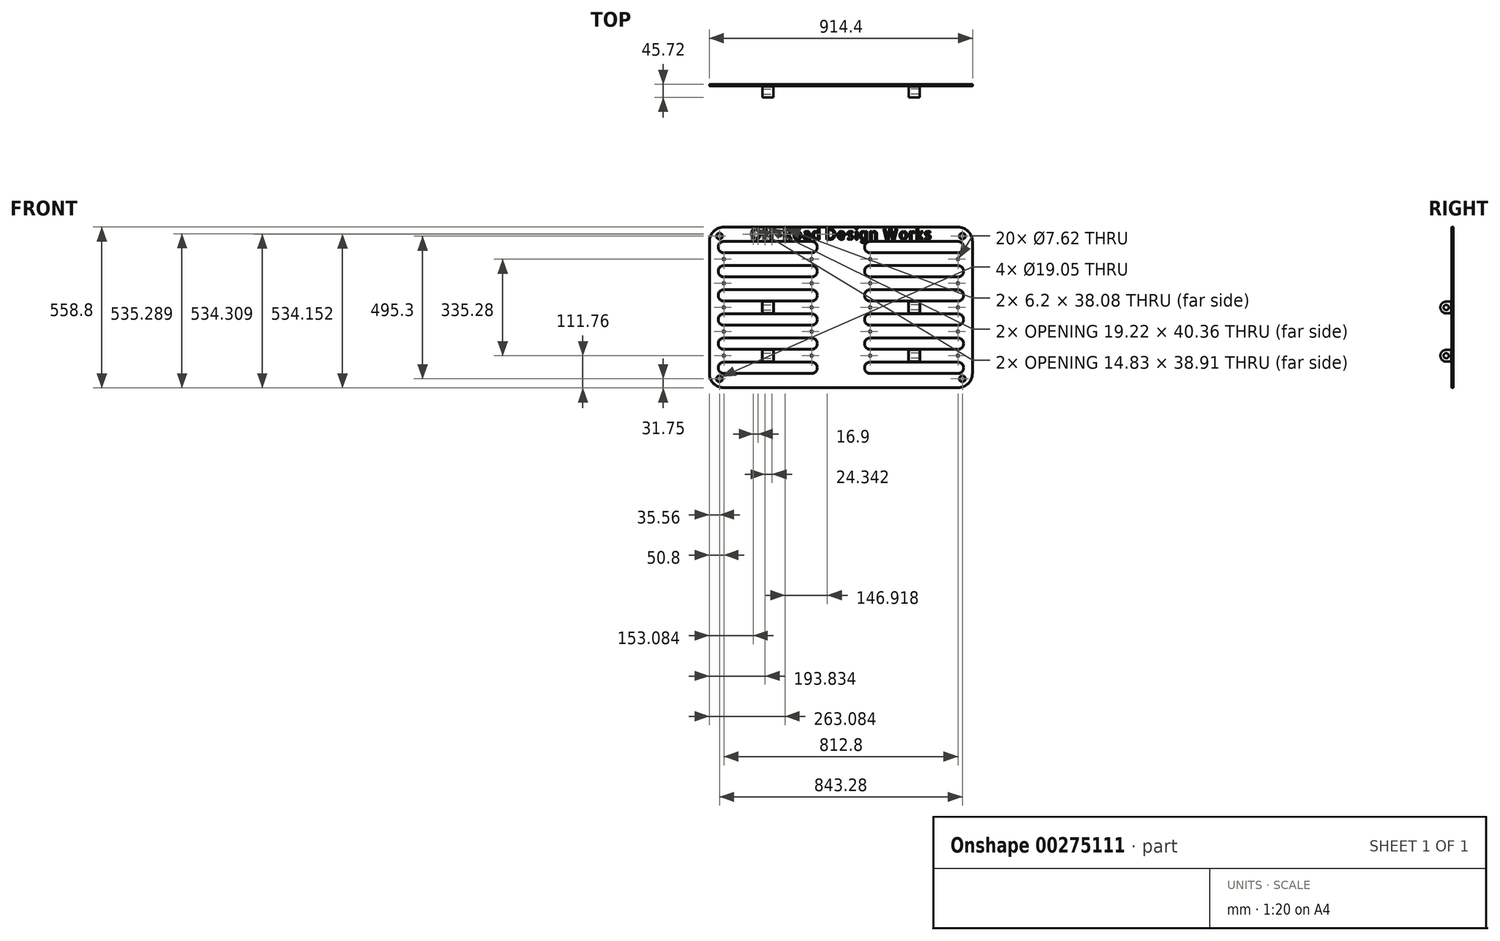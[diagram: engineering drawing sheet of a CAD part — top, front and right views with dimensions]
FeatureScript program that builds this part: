
annotation { "Feature Type Name" : "Feature", "Feature Type Description" : "" }
export const myFeature = defineFeature(function(context is Context, id is Id, definition is map)
    precondition{}
    {
        {
            var Q0;
            Q0=qCreatedBy(makeId("Front.planeOp"),FACE);
            var sketch = newSketch(context, id + "F0", { "sketchPlane" : qUnion([Q0])});
            skLineSegment(sketch, "E0.bottom", {"start": v(406.4, -279.4) * mm, "end": v(-406.4, -279.4) * mm});
            skLineSegment(sketch, "E0.top", {"start": v(406.4, 279.4) * mm, "end": v(-406.4, 279.4) * mm});
            skLineSegment(sketch, "E0.left", {"start": v(457.2, -228.6) * mm, "end": v(457.2, 228.6) * mm});
            skLineSegment(sketch, "E0.right", {"start": v(-457.2, -228.6) * mm, "end": v(-457.2, 228.6) * mm});
            skPoint(sketch, "E0.middle", {"position": v(0, 0) * mm});
            skPoint(sketch, "E1.visualSharp", {"position": v(457.2, 279.4) * mm});
            skArc(sketch, "E1.filletArc", {"start": v(457.2, 228.6) * mm, "mid": v(442.32, 264.52) * mm, "end": v(406.4, 279.4) * mm});
            skPoint(sketch, "E2.visualSharp", {"position": v(-457.2, 279.4) * mm});
            skArc(sketch, "E2.filletArc", {"start": v(-406.4, 279.4) * mm, "mid": v(-442.32, 264.52) * mm, "end": v(-457.2, 228.6) * mm});
            skPoint(sketch, "E3.visualSharp", {"position": v(-457.2, -279.4) * mm});
            skArc(sketch, "E3.filletArc", {"start": v(-457.2, -228.6) * mm, "mid": v(-442.32, -264.52) * mm, "end": v(-406.4, -279.4) * mm});
            skPoint(sketch, "E4.visualSharp", {"position": v(457.2, -279.4) * mm});
            skArc(sketch, "E4.filletArc", {"start": v(406.4, -279.4) * mm, "mid": v(442.32, -264.52) * mm, "end": v(457.2, -228.6) * mm});
            skSolve(sketch);
        }
        {
            var Q0;
            Q0 = qSketchRegion(id + "F0", true);
            extrude(context, id + "F1", {"entities" : qUnion([Q0]), "oppositeDirection" : true, "depth" : 6.35 * mm});
        }
        {
            var Q0;
            Q0=makeQuery(id+"F1.opExtrude","CAP_FACE",FACE,{"disambiguationData":[OSD([sQuery(id+"F0.wireOp",EDGE,"E0.bottom"),sQuery(id+"F0.wireOp",EDGE,"E0.top"),sQuery(id+"F0.wireOp",EDGE,"E0.left"),sQuery(id+"F0.wireOp",EDGE,"E0.right"),sQuery(id+"F0.wireOp",EDGE,"E1.filletArc"),sQuery(id+"F0.wireOp",EDGE,"E2.filletArc"),sQuery(id+"F0.wireOp",EDGE,"E3.filletArc"),sQuery(id+"F0.wireOp",EDGE,"E4.filletArc")])],"isStart":true});
            var sketch = newSketch(context, id + "F2", { "sketchPlane" : qUnion([Q0])});
            skLineSegment(sketch, "E5", {"start": v(0, 0) * mm, "end": v(0, -438.1) * mm, "construction": true});
            skPoint(sketch, "E5.endSnap0", {"position": v(0, -279.4) * mm});
            skLineSegment(sketch, "E6", {"start": v(101.6, 228.6) * mm, "end": v(406.4, 228.6) * mm});
            skArc(sketch, "E7", {"start": v(101.6, 228.6) * mm, "mid": v(82.55, 209.55) * mm, "end": v(101.6, 190.5) * mm});
            skLineSegment(sketch, "E8", {"start": v(101.6, 190.5) * mm, "end": v(406.4, 190.5) * mm});
            skLineSegment(sketch, "E9", {"start": v(254, 228.6) * mm, "end": v(254, 415.14) * mm, "construction": true});
            skPoint(sketch, "E9.endSnap0", {"position": v(254, 190.5) * mm});
            skArc(sketch, "E10.MirrorCS", {"start": v(406.4, 228.6) * mm, "mid": v(425.45, 209.55) * mm, "end": v(406.4, 190.5) * mm});
            skLineSegment(sketch, "E11.0.1.0", {"start": v(101.6, 106.68) * mm, "end": v(406.4, 106.68) * mm});
            skArc(sketch, "E11.0.1.1", {"start": v(101.6, 144.78) * mm, "mid": v(82.55, 125.73) * mm, "end": v(101.6, 106.68) * mm});
            skArc(sketch, "E11.0.1.2", {"start": v(406.4, 144.78) * mm, "mid": v(425.45, 125.73) * mm, "end": v(406.4, 106.68) * mm});
            skLineSegment(sketch, "E11.0.1.3", {"start": v(101.6, 144.78) * mm, "end": v(406.4, 144.78) * mm});
            skLineSegment(sketch, "E11.0.2.0", {"start": v(101.6, 22.86) * mm, "end": v(406.4, 22.86) * mm});
            skArc(sketch, "E11.0.2.1", {"start": v(101.6, 60.96) * mm, "mid": v(82.55, 41.91) * mm, "end": v(101.6, 22.86) * mm});
            skArc(sketch, "E11.0.2.2", {"start": v(406.4, 60.96) * mm, "mid": v(425.45, 41.91) * mm, "end": v(406.4, 22.86) * mm});
            skLineSegment(sketch, "E11.0.2.3", {"start": v(101.6, 60.96) * mm, "end": v(406.4, 60.96) * mm});
            skLineSegment(sketch, "E11.0.3.0", {"start": v(101.6, -60.96) * mm, "end": v(406.4, -60.96) * mm});
            skArc(sketch, "E11.0.3.1", {"start": v(101.6, -22.86) * mm, "mid": v(82.55, -41.9) * mm, "end": v(101.6, -60.96) * mm});
            skArc(sketch, "E11.0.3.2", {"start": v(406.4, -22.86) * mm, "mid": v(425.45, -41.9) * mm, "end": v(406.4, -60.96) * mm});
            skLineSegment(sketch, "E11.0.3.3", {"start": v(101.6, -22.86) * mm, "end": v(406.4, -22.86) * mm});
            skLineSegment(sketch, "E11.0.4.0", {"start": v(101.6, -144.78) * mm, "end": v(406.4, -144.78) * mm});
            skArc(sketch, "E11.0.4.1", {"start": v(101.6, -106.68) * mm, "mid": v(82.55, -125.73) * mm, "end": v(101.6, -144.78) * mm});
            skArc(sketch, "E11.0.4.2", {"start": v(406.4, -106.68) * mm, "mid": v(425.45, -125.73) * mm, "end": v(406.4, -144.78) * mm});
            skLineSegment(sketch, "E11.0.4.3", {"start": v(101.6, -106.68) * mm, "end": v(406.4, -106.68) * mm});
            skLineSegment(sketch, "E11.0.5.0", {"start": v(101.6, -228.6) * mm, "end": v(406.4, -228.6) * mm});
            skArc(sketch, "E11.0.5.1", {"start": v(101.6, -190.5) * mm, "mid": v(82.55, -209.55) * mm, "end": v(101.6, -228.6) * mm});
            skArc(sketch, "E11.0.5.2", {"start": v(406.4, -190.5) * mm, "mid": v(425.45, -209.55) * mm, "end": v(406.4, -228.6) * mm});
            skLineSegment(sketch, "E11.0.5.3", {"start": v(101.6, -190.5) * mm, "end": v(406.4, -190.5) * mm});
            skLineSegment(sketch, "E11.direction1", {"start": v(101.6, 228.6) * mm, "end": v(127, 228.6) * mm, "construction": true});
            skLineSegment(sketch, "E11.direction2", {"start": v(101.6, 228.6) * mm, "end": v(101.6, 144.78) * mm, "construction": true});
            skLineSegment(sketch, "E12.MirrorCS", {"start": v(-101.6, -228.6) * mm, "end": v(-406.4, -228.6) * mm});
            skLineSegment(sketch, "E13.MirrorCS", {"start": v(-101.6, 106.68) * mm, "end": v(-406.4, 106.68) * mm});
            skLineSegment(sketch, "E14.MirrorCS", {"start": v(-101.6, 22.86) * mm, "end": v(-406.4, 22.86) * mm});
            skLineSegment(sketch, "E15.MirrorCS", {"start": v(-101.6, 228.6) * mm, "end": v(-406.4, 228.6) * mm});
            skLineSegment(sketch, "E16.MirrorCS", {"start": v(-101.6, 60.96) * mm, "end": v(-406.4, 60.96) * mm});
            skLineSegment(sketch, "E17.MirrorCS", {"start": v(-101.6, 228.6) * mm, "end": v(-127, 228.6) * mm, "construction": true});
            skArc(sketch, "E18.MirrorCS", {"start": v(-406.4, -190.5) * mm, "mid": v(-425.45, -209.55) * mm, "end": v(-406.4, -228.6) * mm});
            skArc(sketch, "E19.MirrorCS", {"start": v(-101.6, 60.96) * mm, "mid": v(-82.55, 41.91) * mm, "end": v(-101.6, 22.86) * mm});
            skArc(sketch, "E20.MirrorCS", {"start": v(-101.6, 228.6) * mm, "mid": v(-82.55, 209.55) * mm, "end": v(-101.6, 190.5) * mm});
            skLineSegment(sketch, "E21.MirrorCS", {"start": v(-101.6, -60.96) * mm, "end": v(-406.4, -60.96) * mm});
            skLineSegment(sketch, "E22.MirrorCS", {"start": v(-101.6, -106.68) * mm, "end": v(-406.4, -106.68) * mm});
            skLineSegment(sketch, "E23.MirrorCS", {"start": v(-101.6, -22.86) * mm, "end": v(-406.4, -22.86) * mm});
            skArc(sketch, "E24.MirrorCS", {"start": v(-101.6, -106.68) * mm, "mid": v(-82.55, -125.73) * mm, "end": v(-101.6, -144.78) * mm});
            skArc(sketch, "E25.MirrorCS", {"start": v(-406.4, 60.96) * mm, "mid": v(-425.45, 41.91) * mm, "end": v(-406.4, 22.86) * mm});
            skLineSegment(sketch, "E26.MirrorCS", {"start": v(-101.6, 190.5) * mm, "end": v(-406.4, 190.5) * mm});
            skArc(sketch, "E27.MirrorCS", {"start": v(-101.6, -22.86) * mm, "mid": v(-82.55, -41.9) * mm, "end": v(-101.6, -60.96) * mm});
            skArc(sketch, "E28.MirrorCS", {"start": v(-101.6, 144.78) * mm, "mid": v(-82.55, 125.73) * mm, "end": v(-101.6, 106.68) * mm});
            skLineSegment(sketch, "E29.MirrorCS", {"start": v(-101.6, 228.6) * mm, "end": v(-101.6, 144.78) * mm, "construction": true});
            skLineSegment(sketch, "E30.MirrorCS", {"start": v(-101.6, -190.5) * mm, "end": v(-406.4, -190.5) * mm});
            skArc(sketch, "E31.MirrorCS", {"start": v(-101.6, -190.5) * mm, "mid": v(-82.55, -209.55) * mm, "end": v(-101.6, -228.6) * mm});
            skArc(sketch, "E32.MirrorCS", {"start": v(-406.4, 144.78) * mm, "mid": v(-425.45, 125.73) * mm, "end": v(-406.4, 106.68) * mm});
            skArc(sketch, "E33.MirrorCS", {"start": v(-406.4, 228.6) * mm, "mid": v(-425.45, 209.55) * mm, "end": v(-406.4, 190.5) * mm});
            skPoint(sketch, "E34.MirrorP", {"position": v(-254, 190.5) * mm});
            skLineSegment(sketch, "E35.MirrorCS", {"start": v(-101.6, 144.78) * mm, "end": v(-406.4, 144.78) * mm});
            skArc(sketch, "E36.MirrorCS", {"start": v(-406.4, -106.68) * mm, "mid": v(-425.45, -125.73) * mm, "end": v(-406.4, -144.78) * mm});
            skLineSegment(sketch, "E37.MirrorCS", {"start": v(-101.6, -144.78) * mm, "end": v(-406.4, -144.78) * mm});
            skArc(sketch, "E38.MirrorCS", {"start": v(-406.4, -22.86) * mm, "mid": v(-425.45, -41.9) * mm, "end": v(-406.4, -60.96) * mm});
            skSolve(sketch);
        }
        {
            var Q0;
            Q0 = qSketchRegion(id + "F2", true);
            var Q1;
            Q1=makeQuery(id+"F1.opExtrude","CAP_FACE",FACE,{"disambiguationData":[OSD([sQuery(id+"F0.wireOp",EDGE,"E0.bottom"),sQuery(id+"F0.wireOp",EDGE,"E0.top"),sQuery(id+"F0.wireOp",EDGE,"E0.left"),sQuery(id+"F0.wireOp",EDGE,"E0.right"),sQuery(id+"F0.wireOp",EDGE,"E1.filletArc"),sQuery(id+"F0.wireOp",EDGE,"E2.filletArc"),sQuery(id+"F0.wireOp",EDGE,"E3.filletArc"),sQuery(id+"F0.wireOp",EDGE,"E4.filletArc")])],"isStart":false});
            extrude(context, id + "F3", {"entities" : qUnion([Q0]), "operationType" : NewBodyOperationType.REMOVE, "endBound" : BoundingType.UP_TO_SURFACE, "oppositeDirection" : true, "endBoundEntityFace" : qUnion([Q1]), "depth" : 25.4 * mm});
        }
        {
            var Q0;
            Q0=qCreatedBy(makeId("Right.planeOp"),FACE);
            cPlane(context, id + "F4", {"entities" : qUnion([Q0]), "cplaneType" : CPlaneType.OFFSET, "offset" : 254 * mm, "width" : 152.4 * mm, "height" : 152.4 * mm});
        }
        {
            var Q0;
            Q0=qCreatedBy(id+"F4.planeOp",FACE);
            var sketch = newSketch(context, id + "F5", { "sketchPlane" : qUnion([Q0])});
            skLineSegment(sketch, "E39", {"start": v(0, 0) * mm, "end": v(-83.93, 0) * mm, "construction": true});
            skLineSegment(sketch, "E40", {"start": v(0, 20.32) * mm, "end": v(-19.05, 20.32) * mm});
            skLineSegment(sketch, "E41.MirrorCS", {"start": v(0, -20.32) * mm, "end": v(-19.05, -20.32) * mm});
            skArc(sketch, "E42", {"start": v(-19.05, -20.32) * mm, "mid": v(-39.37, 0) * mm, "end": v(-19.05, 20.32) * mm});
            skCircle(sketch, "E43", {"center": v(-19.05, 0) * mm, "radius": 8.9 * mm});
            skLineSegment(sketch, "E44", {"start": v(0, 20.32) * mm, "end": v(0, -20.32) * mm});
            skSolve(sketch);
        }
        {
            var Q0;
            Q0 = qSketchRegion(id + "F5", true);
            extrude(context, id + "F6", {"entities" : qUnion([Q0]), "endBound" : BoundingType.SYMMETRIC, "depth" : 38.1 * mm});
        }
        {
            var Q0;
            Q0=makeQuery(id+"F6.opExtrude","SWEPT_BODY",BODY,{"disambiguationData":[OSD([sQuery(id+"F5.wireOp",EDGE,"E40"),sQuery(id+"F5.wireOp",EDGE,"E41.MirrorCS"),sQuery(id+"F5.wireOp",EDGE,"E42"),sQuery(id+"F5.wireOp",EDGE,"E43"),sQuery(id+"F5.wireOp",EDGE,"E44")])]});
            var Q1;
            Q1=qCreatedBy(makeId("Right.planeOp"),FACE);
            mirror(context, id + "F7", {"entities" : qUnion([Q0]), "mirrorPlane" : qUnion([Q1])});
        }
        {
            var Q0;
            Q0=qCreatedBy(makeId("Top.planeOp"),FACE);
            cPlane(context, id + "F8", {"entities" : qUnion([Q0]), "cplaneType" : CPlaneType.OFFSET, "offset" : 83.82 * mm, "oppositeDirection" : true, "width" : 152.4 * mm, "height" : 152.4 * mm});
        }
        {
            var Q0;
            Q0=makeQuery(id+"F6.opExtrude","SWEPT_BODY",BODY,{"disambiguationData":[OSD([sQuery(id+"F5.wireOp",EDGE,"E40"),sQuery(id+"F5.wireOp",EDGE,"E41.MirrorCS"),sQuery(id+"F5.wireOp",EDGE,"E42"),sQuery(id+"F5.wireOp",EDGE,"E43"),sQuery(id+"F5.wireOp",EDGE,"E44")])]});
            var Q1;
            Q1=makeQuery(id+"F7.opPattern","COPY",BODY,{"derivedFrom":makeQuery(id+"F6.opExtrude","SWEPT_BODY",BODY,{"disambiguationData":[OSD([sQuery(id+"F5.wireOp",EDGE,"E40"),sQuery(id+"F5.wireOp",EDGE,"E41.MirrorCS"),sQuery(id+"F5.wireOp",EDGE,"E42"),sQuery(id+"F5.wireOp",EDGE,"E43"),sQuery(id+"F5.wireOp",EDGE,"E44")])]}),"instanceName":"1"});
            var Q2;
            Q2=qCreatedBy(id+"F8.planeOp",FACE);
            mirror(context, id + "F9", {"operationType" : NewBodyOperationType.ADD, "entities" : qUnion([Q0, Q1]), "mirrorPlane" : qUnion([Q2])});
        }
        {
            var Q0;
            Q0=makeQuery(id+"F1.opExtrude","CAP_FACE",FACE,{"disambiguationData":[OSD([sQuery(id+"F0.wireOp",EDGE,"E0.bottom"),sQuery(id+"F0.wireOp",EDGE,"E0.top"),sQuery(id+"F0.wireOp",EDGE,"E0.left"),sQuery(id+"F0.wireOp",EDGE,"E0.right"),sQuery(id+"F0.wireOp",EDGE,"E1.filletArc"),sQuery(id+"F0.wireOp",EDGE,"E2.filletArc"),sQuery(id+"F0.wireOp",EDGE,"E3.filletArc"),sQuery(id+"F0.wireOp",EDGE,"E4.filletArc")])],"isStart":true});
            var sketch = newSketch(context, id + "F10", { "sketchPlane" : qUnion([Q0])});
            skCircle(sketch, "E45", {"center": v(-421.64, 247.65) * mm, "radius": 9.53 * mm});
            skLineSegment(sketch, "E46", {"start": v(0, 0) * mm, "end": v(0, 190.5) * mm, "construction": true});
            skLineSegment(sketch, "E47", {"start": v(0, 0) * mm, "end": v(-548.2, 0) * mm, "construction": true});
            skPoint(sketch, "E47.endSnap0", {"position": v(-234.95, 0) * mm});
            skCircle(sketch, "E48.MirrorC", {"center": v(421.64, 247.65) * mm, "radius": 9.53 * mm});
            skCircle(sketch, "E49.MirrorC", {"center": v(421.64, -247.65) * mm, "radius": 9.53 * mm});
            skCircle(sketch, "E50.MirrorC", {"center": v(-421.64, -247.65) * mm, "radius": 9.53 * mm});
            skSolve(sketch);
        }
        {
            var Q0;
            Q0 = qSketchRegion(id + "F10", true);
            var Q1;
            Q1=makeQuery(id+"F1.opExtrude","CAP_FACE",FACE,{"disambiguationData":[OSD([sQuery(id+"F0.wireOp",EDGE,"E0.bottom"),sQuery(id+"F0.wireOp",EDGE,"E0.top"),sQuery(id+"F0.wireOp",EDGE,"E0.left"),sQuery(id+"F0.wireOp",EDGE,"E0.right"),sQuery(id+"F0.wireOp",EDGE,"E1.filletArc"),sQuery(id+"F0.wireOp",EDGE,"E2.filletArc"),sQuery(id+"F0.wireOp",EDGE,"E3.filletArc"),sQuery(id+"F0.wireOp",EDGE,"E4.filletArc")])],"isStart":false});
            extrude(context, id + "F11", {"entities" : qUnion([Q0]), "operationType" : NewBodyOperationType.REMOVE, "endBound" : BoundingType.UP_TO_SURFACE, "oppositeDirection" : true, "endBoundEntityFace" : qUnion([Q1]), "depth" : 25.4 * mm});
        }
        {
            var Q0;
            Q0=makeQuery(id+"F1.opExtrude","CAP_FACE",FACE,{"disambiguationData":[OSD([sQuery(id+"F0.wireOp",EDGE,"E0.bottom"),sQuery(id+"F0.wireOp",EDGE,"E0.top"),sQuery(id+"F0.wireOp",EDGE,"E0.left"),sQuery(id+"F0.wireOp",EDGE,"E0.right"),sQuery(id+"F0.wireOp",EDGE,"E1.filletArc"),sQuery(id+"F0.wireOp",EDGE,"E2.filletArc"),sQuery(id+"F0.wireOp",EDGE,"E3.filletArc"),sQuery(id+"F0.wireOp",EDGE,"E4.filletArc")])],"isStart":true});
            chamfer(context, id + "F12", {"entities" : qUnion([Q0]), "width" : 1.27 * mm, "tangentPropagation" : true});
        }
        {
            var Q0;
            Q0=makeQuery(id+"F1.opExtrude","CAP_FACE",FACE,{"disambiguationData":[OSD([sQuery(id+"F0.wireOp",EDGE,"E0.bottom"),sQuery(id+"F0.wireOp",EDGE,"E0.top"),sQuery(id+"F0.wireOp",EDGE,"E0.left"),sQuery(id+"F0.wireOp",EDGE,"E0.right"),sQuery(id+"F0.wireOp",EDGE,"E1.filletArc"),sQuery(id+"F0.wireOp",EDGE,"E2.filletArc"),sQuery(id+"F0.wireOp",EDGE,"E3.filletArc"),sQuery(id+"F0.wireOp",EDGE,"E4.filletArc")])],"isStart":true});
            var sketch = newSketch(context, id + "F13", { "sketchPlane" : qUnion([Q0])});
            skText(sketch, "E51", { "text": "Off-Road Design Works", "fontName": "AllertaStencil-Regular.ttf"});
            skLineSegment(sketch, "E52", {"start": v(0, 0) * mm, "end": v(0, 235.71) * mm, "construction": true});
            const initialGuessF13  = {"E51": [-0.31551, 0.23571, 1, 0, 0.0381]};
            skSetInitialGuess(sketch, initialGuessF13);
            skSolve(sketch);
        }
        {
            var Q0;
            Q0 = qSketchRegion(id + "F13", true);
            var Q1;
            Q1=makeQuery(id+"F1.opExtrude","CAP_FACE",FACE,{"disambiguationData":[OSD([sQuery(id+"F0.wireOp",EDGE,"E0.bottom"),sQuery(id+"F0.wireOp",EDGE,"E0.top"),sQuery(id+"F0.wireOp",EDGE,"E0.left"),sQuery(id+"F0.wireOp",EDGE,"E0.right"),sQuery(id+"F0.wireOp",EDGE,"E1.filletArc"),sQuery(id+"F0.wireOp",EDGE,"E2.filletArc"),sQuery(id+"F0.wireOp",EDGE,"E3.filletArc"),sQuery(id+"F0.wireOp",EDGE,"E4.filletArc")])],"isStart":false});
            extrude(context, id + "F14", {"entities" : qUnion([Q0]), "operationType" : NewBodyOperationType.REMOVE, "endBound" : BoundingType.UP_TO_SURFACE, "oppositeDirection" : true, "endBoundEntityFace" : qUnion([Q1]), "depth" : 25.4 * mm});
        }
        {
            var Q0;
            Q0=makeQuery(id+"F1.opExtrude","CAP_FACE",FACE,{"disambiguationData":[OSD([sQuery(id+"F0.wireOp",EDGE,"E0.bottom"),sQuery(id+"F0.wireOp",EDGE,"E0.top"),sQuery(id+"F0.wireOp",EDGE,"E0.left"),sQuery(id+"F0.wireOp",EDGE,"E0.right"),sQuery(id+"F0.wireOp",EDGE,"E1.filletArc"),sQuery(id+"F0.wireOp",EDGE,"E2.filletArc"),sQuery(id+"F0.wireOp",EDGE,"E3.filletArc"),sQuery(id+"F0.wireOp",EDGE,"E4.filletArc")])],"isStart":true});
            var sketch = newSketch(context, id + "F15", { "sketchPlane" : qUnion([Q0])});
            skCircle(sketch, "E53", {"center": v(406.4, 167.64) * mm, "radius": 3.81 * mm});
            skLineSegment(sketch, "E54", {"start": v(254, 189.23) * mm, "end": v(254, 127.25) * mm, "construction": true});
            skCircle(sketch, "E55.MirrorC", {"center": v(101.6, 167.64) * mm, "radius": 3.81 * mm});
            skCircle(sketch, "E56.0.1.0", {"center": v(101.6, 83.82) * mm, "radius": 3.81 * mm});
            skCircle(sketch, "E56.0.1.1", {"center": v(406.4, 83.82) * mm, "radius": 3.81 * mm});
            skCircle(sketch, "E56.0.2.0", {"center": v(101.6, 0) * mm, "radius": 3.81 * mm});
            skCircle(sketch, "E56.0.2.1", {"center": v(406.4, 0) * mm, "radius": 3.81 * mm});
            skCircle(sketch, "E56.0.3.0", {"center": v(101.6, -83.82) * mm, "radius": 3.81 * mm});
            skCircle(sketch, "E56.0.3.1", {"center": v(406.4, -83.82) * mm, "radius": 3.81 * mm});
            skCircle(sketch, "E56.0.4.0", {"center": v(101.6, -167.64) * mm, "radius": 3.81 * mm});
            skCircle(sketch, "E56.0.4.1", {"center": v(406.4, -167.64) * mm, "radius": 3.81 * mm});
            skLineSegment(sketch, "E56.direction1", {"start": v(101.6, 167.64) * mm, "end": v(127, 167.64) * mm, "construction": true});
            skLineSegment(sketch, "E56.direction2", {"start": v(101.6, 167.64) * mm, "end": v(101.6, 83.82) * mm, "construction": true});
            skLineSegment(sketch, "E57", {"start": v(0, 0) * mm, "end": v(0, -99.16) * mm, "construction": true});
            skCircle(sketch, "E58.MirrorC", {"center": v(-406.4, -167.64) * mm, "radius": 3.81 * mm});
            skCircle(sketch, "E59.MirrorC", {"center": v(-406.4, 0) * mm, "radius": 3.81 * mm});
            skCircle(sketch, "E60.MirrorC", {"center": v(-406.4, -83.82) * mm, "radius": 3.81 * mm});
            skCircle(sketch, "E61.MirrorC", {"center": v(-406.4, 83.82) * mm, "radius": 3.81 * mm});
            skCircle(sketch, "E62.MirrorC", {"center": v(-406.4, 167.64) * mm, "radius": 3.81 * mm});
            skLineSegment(sketch, "E63.MirrorCS", {"start": v(-101.6, 167.64) * mm, "end": v(-101.6, 83.82) * mm, "construction": true});
            skCircle(sketch, "E64.MirrorC", {"center": v(-101.6, 167.64) * mm, "radius": 3.81 * mm});
            skCircle(sketch, "E65.MirrorC", {"center": v(-101.6, -83.82) * mm, "radius": 3.81 * mm});
            skCircle(sketch, "E66.MirrorC", {"center": v(-101.6, -167.64) * mm, "radius": 3.81 * mm});
            skLineSegment(sketch, "E67.MirrorCS", {"start": v(-101.6, 167.64) * mm, "end": v(-127, 167.64) * mm, "construction": true});
            skCircle(sketch, "E68.MirrorC", {"center": v(-101.6, 83.82) * mm, "radius": 3.81 * mm});
            skCircle(sketch, "E69.MirrorC", {"center": v(-101.6, 0) * mm, "radius": 3.81 * mm});
            skSolve(sketch);
        }
        {
            var Q0;
            Q0 = qSketchRegion(id + "F15", true);
            var Q1;
            Q1=makeQuery(id+"F1.opExtrude","CAP_FACE",FACE,{"disambiguationData":[OSD([sQuery(id+"F0.wireOp",EDGE,"E0.bottom"),sQuery(id+"F0.wireOp",EDGE,"E0.top"),sQuery(id+"F0.wireOp",EDGE,"E0.left"),sQuery(id+"F0.wireOp",EDGE,"E0.right"),sQuery(id+"F0.wireOp",EDGE,"E1.filletArc"),sQuery(id+"F0.wireOp",EDGE,"E2.filletArc"),sQuery(id+"F0.wireOp",EDGE,"E3.filletArc"),sQuery(id+"F0.wireOp",EDGE,"E4.filletArc")])],"isStart":false});
            extrude(context, id + "F16", {"entities" : qUnion([Q0]), "operationType" : NewBodyOperationType.REMOVE, "endBound" : BoundingType.UP_TO_SURFACE, "oppositeDirection" : true, "endBoundEntityFace" : qUnion([Q1]), "depth" : 25.4 * mm});
        }
    });
